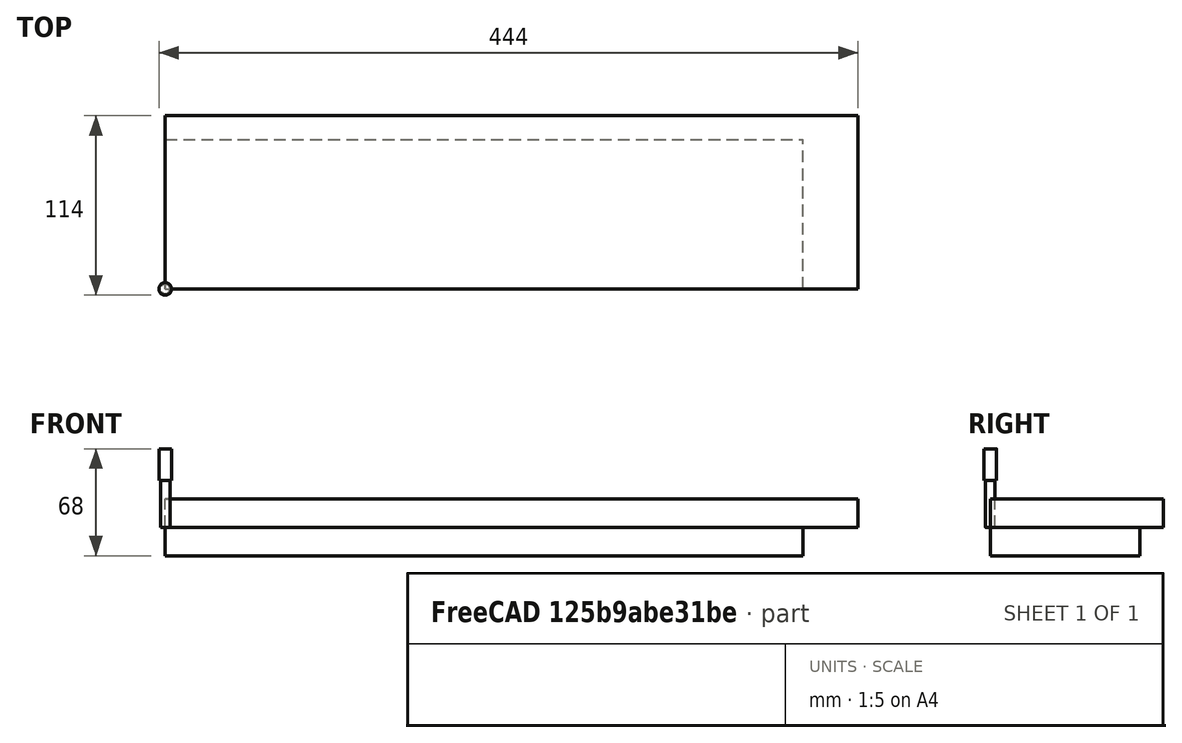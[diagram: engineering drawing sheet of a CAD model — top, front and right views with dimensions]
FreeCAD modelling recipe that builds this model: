
FCSTD DOCUMENT  (FreeCAD 0.22R34789 (Git))
Label: base
License: All rights reserved
LicenseURL: http://en.wikipedia.org/wiki/All_rights_reserved
objects: App::FeaturePython×21, Path::FeaturePython×16, Part::FeaturePython×8, App::DocumentObjectGroup×3, Sketcher::SketchObject×1, PartDesign::Pad×1, PartDesign::Body×1, Mesh::FeaturePython×1
note: 25 computed .brp shape members not serialized (recipe doc carries the construction recipe); baked Part::Feature solids carry a one-line shape summary decoded from their .brp

FEATURE [Sketcher::SketchObject] Sketch
  FullyConstrained = true
  MapMode = 5
  Support = -> [XY_Plane]
  sketch-geometry (4):
    g0: LineSegment StartX=0 StartY=0 StartZ=0 EndX=440 EndY=0 EndZ=0
    g1: LineSegment StartX=440 StartY=0 StartZ=0 EndX=440 EndY=110 EndZ=0
    g2: LineSegment StartX=440 StartY=110 StartZ=0 EndX=0 EndY=110 EndZ=0
    g3: LineSegment StartX=0 StartY=110 StartZ=0 EndX=0 EndY=0 EndZ=0
  constraints (11):
    c: Coincident(g0,g1)
    c: Coincident(g1,g2)
    c: Coincident(g2,g3)
    c: Coincident(g3,g0)
    c: Horizontal(g0)
    c: Horizontal(g2)
    c: Vertical(g1)
    c: Vertical(g3)
    c: Coincident(g0,g-1)
    c: DistanceY(g3,g3) = 110
    c: DistanceX(g2,g2) = 440
FEATURE [PartDesign::Pad] Pad
  Direction = (0,0,1)
  Length = 18
  Length2 = 10
  Profile = -> Sketch
  ReferenceAxis = -> Sketch [N_Axis]
  Type = 0
FEATURE [PartDesign::Body] Body
  Group = -> [Sketch,Pad]
  Origin = -> Origin
  Tip = -> Pad
FEATURE [Part::FeaturePython] Body_001  # a2plus imported part (geometry in sourceFile) (typed FeaturePython)
  a2p_Version = 0.4.61
  fixedPosition = true
  localSourceObject = Body
  objectType = a2pPart
  sourceFile = converted
  subassemblyImport = false
  timeLastImport = 1.69957e+09
  updateColors = true
FEATURE [Part::FeaturePython] b_drill_press_table_001_  label="drill_press_table_base_side_left_001"  # a2plus imported part (geometry in sourceFile) (typed FeaturePython)
  Placement = pos=(362,3.66479e-06,131) rot=(0.57735,-0.57735,0.57735;2.0944rad)
  a2p_Version = 0.4.61
  fixedPosition = false
  objectType = a2pPart
  sourceFile = ./../drill_press_table.FCStd
  sourcePart = base_side_left
  subassemblyImport = false
  timeLastImport = 1.69948e+09
  updateColors = true
FEATURE [Part::FeaturePython] b_drill_press_table_001_001  label="drill_press_table_vacuum_port_001"  # a2plus imported part (geometry in sourceFile) (typed FeaturePython)
  Placement = pos=(310,-276.5,149) rot=(0,-1,0;1.5708rad)
  a2p_Version = 0.4.61
  fixedPosition = false
  objectType = a2pPart
  sourceFile = ./../drill_press_table.FCStd
  sourcePart = vacuum_port
  subassemblyImport = false
  timeLastImport = 1.69948e+09
  updateColors = true
FEATURE [App::FeaturePython] planesParallel_001  label="planesParallel_001__Body_001"  # a2plus constraint (typed FeaturePython)
  Object1 = b_drill_press_table_001_
  Object2 = Body_001
  ParentTreeObject = -> b_drill_press_table_001_
  SubElement1 = Face2
  SubElement2 = Face6
  Suppressed = false
  Type = planesParallel
  directionConstraint = 0
FEATURE [App::FeaturePython] planesParallel_001_mirror  label="planesParallel_001__drill_press_table_base_side_left_001"  # a2plus constraint (typed FeaturePython)
  Object1 = b_drill_press_table_001_
  Object2 = Body_001
  ParentTreeObject = -> Body_001
  SubElement1 = Face2
  SubElement2 = Face6
  Suppressed = false
  Type = planesParallel
  directionConstraint = 0
FEATURE [App::FeaturePython] planesParallel_002  label="planesParallel_002__Body_001"  # a2plus constraint (typed FeaturePython)
  Object1 = b_drill_press_table_001_
  Object2 = Body_001
  ParentTreeObject = -> b_drill_press_table_001_
  SubElement1 = Face3
  SubElement2 = Face1
  Suppressed = false
  Type = planesParallel
  directionConstraint = 0
FEATURE [App::FeaturePython] planesParallel_002_mirror  label="planesParallel_002__drill_press_table_base_side_left_001"  # a2plus constraint (typed FeaturePython)
  Object1 = b_drill_press_table_001_
  Object2 = Body_001
  ParentTreeObject = -> Body_001
  SubElement1 = Face3
  SubElement2 = Face1
  Suppressed = false
  Type = planesParallel
  directionConstraint = 0
FEATURE [App::FeaturePython] planesParallel_003  label="planesParallel_003__Body_001"  # a2plus constraint (typed FeaturePython)
  Object1 = b_drill_press_table_001_
  Object2 = Body_001
  ParentTreeObject = -> b_drill_press_table_001_
  SubElement1 = Face2
  SubElement2 = Face5
  Suppressed = false
  Type = planesParallel
  directionConstraint = 0
FEATURE [App::FeaturePython] planesParallel_003_mirror  label="planesParallel_003__drill_press_table_base_side_left_001"  # a2plus constraint (typed FeaturePython)
  Object1 = b_drill_press_table_001_
  Object2 = Body_001
  ParentTreeObject = -> Body_001
  SubElement1 = Face2
  SubElement2 = Face5
  Suppressed = false
  Type = planesParallel
  directionConstraint = 0
FEATURE [App::FeaturePython] planeCoincident_001  label="planeCoincident_001__Body_001"  # a2plus constraint (typed FeaturePython)
  Object1 = b_drill_press_table_001_
  Object2 = Body_001
  ParentTreeObject = -> b_drill_press_table_001_
  SubElement1 = Face2
  SubElement2 = Face5
  Suppressed = false
  Type = plane
  directionConstraint = 0
  offset = 0
FEATURE [App::FeaturePython] planeCoincident_001_mirror  label="planeCoincident_001__drill_press_table_base_side_left_001"  # a2plus constraint (typed FeaturePython)
  Object1 = b_drill_press_table_001_
  Object2 = Body_001
  ParentTreeObject = -> Body_001
  SubElement1 = Face2
  SubElement2 = Face5
  Suppressed = false
  Type = plane
  directionConstraint = 0
  offset = 0
FEATURE [App::FeaturePython] planeCoincident_002  label="planeCoincident_002__Body_001"  # a2plus constraint (typed FeaturePython)
  Object1 = b_drill_press_table_001_
  Object2 = Body_001
  ParentTreeObject = -> b_drill_press_table_001_
  SubElement1 = Face8
  SubElement2 = Face1
  Suppressed = false
  Type = plane
  directionConstraint = 1
  offset = 0
FEATURE [App::FeaturePython] planeCoincident_002_mirror  label="planeCoincident_002__drill_press_table_base_side_left_001"  # a2plus constraint (typed FeaturePython)
  Object1 = b_drill_press_table_001_
  Object2 = Body_001
  ParentTreeObject = -> Body_001
  SubElement1 = Face8
  SubElement2 = Face1
  Suppressed = false
  Type = plane
  directionConstraint = 1
  offset = 0
FEATURE [App::FeaturePython] planeCoincident_003  label="planeCoincident_003__Body_001"  # a2plus constraint (typed FeaturePython)
  Object1 = b_drill_press_table_001_
  Object2 = Body_001
  ParentTreeObject = -> b_drill_press_table_001_
  SubElement1 = Face1
  SubElement2 = Face4
  Suppressed = false
  Type = plane
  directionConstraint = 1
  offset = 0
FEATURE [App::FeaturePython] planeCoincident_003_mirror  label="planeCoincident_003__drill_press_table_base_side_left_001"  # a2plus constraint (typed FeaturePython)
  Object1 = b_drill_press_table_001_
  Object2 = Body_001
  ParentTreeObject = -> Body_001
  SubElement1 = Face1
  SubElement2 = Face4
  Suppressed = false
  Type = plane
  directionConstraint = 1
  offset = 0
FEATURE [App::FeaturePython] planesParallel_004  label="planesParallel_004__Body_001"  # a2plus constraint (typed FeaturePython)
  Object1 = b_drill_press_table_001_001
  Object2 = Body_001
  ParentTreeObject = -> b_drill_press_table_001_001
  SubElement1 = Face4
  SubElement2 = Face6
  Suppressed = false
  Type = planesParallel
  directionConstraint = 0
FEATURE [App::FeaturePython] planesParallel_004_mirror  label="planesParallel_004__drill_press_table_vacuum_port_001"  # a2plus constraint (typed FeaturePython)
  Object1 = b_drill_press_table_001_001
  Object2 = Body_001
  ParentTreeObject = -> Body_001
  SubElement1 = Face4
  SubElement2 = Face6
  Suppressed = false
  Type = planesParallel
  directionConstraint = 0
FEATURE [App::FeaturePython] planeCoincident_004  label="planeCoincident_004__Body_001"  # a2plus constraint (typed FeaturePython)
  Object1 = b_drill_press_table_001_001
  Object2 = Body_001
  ParentTreeObject = -> b_drill_press_table_001_001
  SubElement1 = Face6
  SubElement2 = Face1
  Suppressed = false
  Type = plane
  directionConstraint = 1
  offset = 0
FEATURE [App::FeaturePython] planeCoincident_004_mirror  label="planeCoincident_004__drill_press_table_vacuum_port_001"  # a2plus constraint (typed FeaturePython)
  Object1 = b_drill_press_table_001_001
  Object2 = Body_001
  ParentTreeObject = -> Body_001
  SubElement1 = Face6
  SubElement2 = Face1
  Suppressed = false
  Type = plane
  directionConstraint = 1
  offset = 0
FEATURE [App::FeaturePython] planeCoincident_005  label="planeCoincident_005__Body_001"  # a2plus constraint (typed FeaturePython)
  Object1 = b_drill_press_table_001_001
  Object2 = Body_001
  ParentTreeObject = -> b_drill_press_table_001_001
  SubElement1 = Face4
  SubElement2 = Face5
  Suppressed = false
  Type = plane
  directionConstraint = 0
  offset = 0
FEATURE [App::FeaturePython] planeCoincident_005_mirror  label="planeCoincident_005__drill_press_table_vacuum_port_001"  # a2plus constraint (typed FeaturePython)
  Object1 = b_drill_press_table_001_001
  Object2 = Body_001
  ParentTreeObject = -> Body_001
  SubElement1 = Face4
  SubElement2 = Face5
  Suppressed = false
  Type = plane
  directionConstraint = 0
  offset = 0
FEATURE [App::FeaturePython] planeCoincident_006  label="planeCoincident_006__drill_press_table_base_side_left_001"  # a2plus constraint (typed FeaturePython)
  Object1 = b_drill_press_table_001_001
  Object2 = b_drill_press_table_001_
  ParentTreeObject = -> b_drill_press_table_001_001
  SubElement1 = Face2
  SubElement2 = Face9
  Suppressed = false
  Type = plane
  directionConstraint = 1
  offset = -10
FEATURE [App::FeaturePython] planeCoincident_006_mirror  label="planeCoincident_006__drill_press_table_vacuum_port_001"  # a2plus constraint (typed FeaturePython)
  Object1 = b_drill_press_table_001_001
  Object2 = b_drill_press_table_001_
  ParentTreeObject = -> b_drill_press_table_001_
  SubElement1 = Face2
  SubElement2 = Face9
  Suppressed = false
  Type = plane
  directionConstraint = 1
  offset = -10
FEATURE [App::FeaturePython] SetupSheet  # Path/CAM operation (typed FeaturePython)
  ClearanceHeightExpression = OpStockZMax+SetupSheet.ClearanceHeightOffset
  ClearanceHeightOffset = 5
  CoolantMode = 0
  CoolantModes = None | Flood | Mist
  FinalDepthExpression = OpFinalDepth
  HorizRapid = 0
  SafeHeightExpression = OpStockZMax+SetupSheet.SafeHeightOffset
  SafeHeightOffset = 3
  StartDepthExpression = OpStartDepth
  StepDownExpression = OpToolDiameter/3
  VertRapid = 0
FEATURE [Part::FeaturePython] Clone  label="Model-drill_press_table_base_side_left_001"  # Draft clone (typed FeaturePython)
  AttacherType = Attacher::AttachEngine3D
  Fuse = false
  Objects = -> [b_drill_press_table_001_]
  PathResource = Model
  Placement = pos=(372,10,113) rot=(0.57735,-0.57735,0.57735;2.0944rad)
  Scale = (1,1,1)
FEATURE [Part::FeaturePython] Clone001  label="Model-drill_press_table_vacuum_port_001"  # Draft clone (typed FeaturePython)
  AttacherType = Attacher::AttachEngine3D
  Fuse = false
  Objects = -> [b_drill_press_table_001_001]
  PathResource = Model
  Placement = pos=(320,-266.5,131) rot=(0,-1,0;1.5708rad)
  Scale = (1,1,1)
FEATURE [App::DocumentObjectGroup] Model
  Group = -> [Clone,Clone001]
FEATURE [Part::FeaturePython] Stock  # WARN: FeaturePython — macro-defined, semantics opaque (R4)
  Base = -> Model
  ExtXneg = 10
  ExtXpos = 10
  ExtYneg = 10
  ExtYpos = 10
  ExtZneg = 0
  ExtZpos = 0
  Placement = pos=(10,10,-18) rot=(0,0,1;0rad)
  StockType = FromBase
FEATURE [Part::FeaturePython] ToolBit001  label="6 mm endmill"  # Path/CAM toolbit (typed FeaturePython)
  BitPropertyNames = Chipload | CuttingEdgeHeight | Diameter | Flutes | Length | Material | ShankDiameter | SpindleDirection
  BitShape = <userpath>/.local/share/FreeCAD/Macro/Tools/Shape/endmill.fcstd
  Chipload = 0
  CuttingEdgeHeight = 30
  Diameter = 6
  File = <userpath>/.local/share/FreeCAD/Macro/Tools/Bit/fbe41074-7b3e-11ee-b334-02422c3495f2.fctb
  Flutes = 2
  Length = 50
  Material = 0
  ShankDiameter = 8
  ShapeName = endmill
  SpindleDirection = 0
FEATURE [Path::FeaturePython] TC__6_mm_endmill  label="TC: 6 mm endmill"  # Path/CAM operation (typed FeaturePython)
  HorizFeed = 20
  HorizRapid = 0
  SpindleDir = 0
  SpindleSpeed = 0
  Tool = -> ToolBit001
  ToolNumber = 16
  VertFeed = 1
  VertRapid = 0
  expr: HorizRapid = SetupSheet.HorizRapid
  expr: VertRapid = SetupSheet.VertRapid
FEATURE [Path::FeaturePython] Pocket_Shape  # Path/CAM operation (typed FeaturePython)
  Active = true
  AreaParams:
    Tolerance = 1e-07
    FitArcs = True
    Simplify = False
    CleanDistance = 0.0
    Accuracy = 0.01
    Unit = 1.0
    MinArcPoints = 4
    MaxArcPoints = 100
    ClipperScale = 10000000.0
    Fill = 0
    Coplanar = 0
    Reorient = True
    Outline = False
    Explode = False
    OpenMode = 0
    Deflection = 0.01
    SubjectFill = 0
    ClipFill = 0
    Offset = 0.0
    ExtraPass = 0
    Stepover = 0.0
    LastStepover = 0.0
    JoinType = 0
    EndType = 0
    MiterLimit = 2.0
    RoundPrecision = 0.0
    PocketMode = 2
    ToolRadius = 3.0
    PocketExtraOffset = -1.0
    PocketStepover = 4.800000000000001
    PocketLastStepover = 0.0
    FromCenter = True
    Angle = 45.0
    AngleShift = 0.0
    Shift = 0.0
    Thicken = False
    SectionCount = -1
    Stepdown = 1.0
    SectionOffset = 0.0
    SectionTolerance = 1e-07
    SectionMode = 2
    Project = False
  Base = -> [Clone]
  ClearanceHeight = 5
  CoolantMode = 0
  CutMode = 0
  CycleTime = 00:08:09
  ExtensionCorners = true
  ExtensionFeature = -> [Clone]
  ExtensionLengthDefault = 3
  ExtraOffset = -1
  FinalDepth = -6.5
  FinishDepth = 0
  KeepToolDown = false
  MinTravel = false
  OffsetPattern = 1
  OpFinalDepth = -6
  OpStartDepth = 9.95e-14
  OpStockZMax = 8.17e-14
  OpStockZMin = -18
  OpToolDiameter = 6
  PathParams = {'orientation': 1, 'feedrate': 20.0, 'feedrate_v': 1.0, 'verbose': True, 'resume_height': 3.0000000000000817, 'retraction': 5.000000000000082, 'return_end': True, 'preamble': False}
  PocketLastStepOver = 0
  SafeHeight = 3
  SplitArcs = false
  StartAt = 0
  StartDepth = 9.95e-14
  StartPoint = (0,0,0)
  StepDown = 2
  StepOver = 80
  ToolController = -> TC__6_mm_endmill
  UseOutline = false
  UseRestMachining = false
  UseStartPoint = false
  ZigZagAngle = 45
  expr: ClearanceHeight = OpStockZMax + SetupSheet.ClearanceHeightOffset
  expr: ExtensionLengthDefault = OpToolDiameter / 2
  expr: FinalDepth = OpFinalDepth - 0.5 mm
  expr: SafeHeight = OpStockZMax + SetupSheet.SafeHeightOffset
  expr: StartDepth = OpStartDepth
  expr: StepDown = OpToolDiameter / 3
FEATURE [Path::FeaturePython] Pocket_Shape001  # Path/CAM operation (typed FeaturePython)
  Active = true
  AreaParams:
    Tolerance = 1e-07
    FitArcs = True
    Simplify = False
    CleanDistance = 0.0
    Accuracy = 0.01
    Unit = 1.0
    MinArcPoints = 4
    MaxArcPoints = 100
    ClipperScale = 10000000.0
    Fill = 0
    Coplanar = 0
    Reorient = True
    Outline = False
    Explode = False
    OpenMode = 0
    Deflection = 0.01
    SubjectFill = 0
    ClipFill = 0
    Offset = 0.0
    ExtraPass = 0
    Stepover = 0.0
    LastStepover = 0.0
    JoinType = 0
    EndType = 0
    MiterLimit = 2.0
    RoundPrecision = 0.0
    PocketMode = 2
    ToolRadius = 3.0
    PocketExtraOffset = -0.8
    PocketStepover = 4.800000000000001
    PocketLastStepover = 0.0
    FromCenter = True
    Angle = 45.0
    AngleShift = 0.0
    Shift = 0.0
    Thicken = False
    SectionCount = -1
    Stepdown = 1.0
    SectionOffset = 0.0
    SectionTolerance = 1e-07
    SectionMode = 2
    Project = False
  Base = -> [Clone]
  ClearanceHeight = 5
  CoolantMode = 0
  CutMode = 0
  CycleTime = 00:06:03
  ExtensionCorners = true
  ExtensionFeature = -> [Clone]
  ExtensionLengthDefault = 4
  ExtraOffset = -0.8
  FinalDepth = -6.5
  FinishDepth = 0
  KeepToolDown = false
  MinTravel = false
  OffsetPattern = 1
  OpFinalDepth = -6
  OpStartDepth = 9.95e-14
  OpStockZMax = 8.17e-14
  OpStockZMin = -18
  OpToolDiameter = 6
  PathParams = {'orientation': 1, 'feedrate': 20.0, 'feedrate_v': 1.0, 'verbose': True, 'resume_height': 3.0000000000000817, 'retraction': 5.000000000000082, 'return_end': True, 'preamble': False}
  PocketLastStepOver = 0
  SafeHeight = 3
  SplitArcs = false
  StartAt = 0
  StartDepth = 9.95e-14
  StartPoint = (0,0,0)
  StepDown = 2
  StepOver = 80
  ToolController = -> TC__6_mm_endmill
  UseOutline = false
  UseRestMachining = false
  UseStartPoint = false
  ZigZagAngle = 45
  expr: ClearanceHeight = OpStockZMax + SetupSheet.ClearanceHeightOffset
  expr: ExtensionLengthDefault = OpToolDiameter / 2 + 1 mm
  expr: FinalDepth = OpFinalDepth - 0.5 mm
  expr: SafeHeight = OpStockZMax + SetupSheet.SafeHeightOffset
  expr: StartDepth = OpStartDepth
  expr: StepDown = OpToolDiameter / 3
FEATURE [Path::FeaturePython] Pocket_Shape002  # Path/CAM operation (typed FeaturePython)
  Active = true
  AreaParams:
    Tolerance = 1e-07
    FitArcs = True
    Simplify = False
    CleanDistance = 0.0
    Accuracy = 0.01
    Unit = 1.0
    MinArcPoints = 4
    MaxArcPoints = 100
    ClipperScale = 10000000.0
    Fill = 0
    Coplanar = 0
    Reorient = True
    Outline = False
    Explode = False
    OpenMode = 0
    Deflection = 0.01
    SubjectFill = 0
    ClipFill = 0
    Offset = 0.0
    ExtraPass = 0
    Stepover = 0.0
    LastStepover = 0.0
    JoinType = 0
    EndType = 0
    MiterLimit = 2.0
    RoundPrecision = 0.0
    PocketMode = 2
    ToolRadius = 3.0
    PocketExtraOffset = -0.6
    PocketStepover = 4.800000000000001
    PocketLastStepover = 0.0
    FromCenter = True
    Angle = 45.0
    AngleShift = 0.0
    Shift = 0.0
    Thicken = False
    SectionCount = -1
    Stepdown = 1.0
    SectionOffset = 0.0
    SectionTolerance = 1e-07
    SectionMode = 2
    Project = False
  Base = -> [Clone]
  ClearanceHeight = 5
  CoolantMode = 0
  CutMode = 0
  CycleTime = 00:06:39
  ExtensionCorners = true
  ExtensionFeature = -> [Clone]
  ExtensionLengthDefault = 3
  ExtraOffset = -0.6
  FinalDepth = -6.5
  FinishDepth = 0
  KeepToolDown = false
  MinTravel = false
  OffsetPattern = 1
  OpFinalDepth = -6
  OpStartDepth = 8.17e-14
  OpStockZMax = 8.17e-14
  OpStockZMin = -18
  OpToolDiameter = 6
  PathParams = {'orientation': 1, 'feedrate': 20.0, 'feedrate_v': 1.0, 'verbose': True, 'resume_height': 3.0000000000000817, 'retraction': 5.000000000000082, 'return_end': True, 'preamble': False}
  PocketLastStepOver = 0
  SafeHeight = 3
  SplitArcs = false
  StartAt = 0
  StartDepth = 8.17e-14
  StartPoint = (0,0,0)
  StepDown = 2
  StepOver = 80
  ToolController = -> TC__6_mm_endmill
  UseOutline = false
  UseRestMachining = false
  UseStartPoint = false
  ZigZagAngle = 45
  expr: ClearanceHeight = OpStockZMax + SetupSheet.ClearanceHeightOffset
  expr: ExtensionLengthDefault = OpToolDiameter / 2
  expr: FinalDepth = OpFinalDepth - 0.5 mm
  expr: SafeHeight = OpStockZMax + SetupSheet.SafeHeightOffset
  expr: StartDepth = OpStartDepth
  expr: StepDown = OpToolDiameter / 3
FEATURE [Path::FeaturePython] Profile  # Path/CAM operation (typed FeaturePython)
  Active = true
  AreaParams:
    Tolerance = 1e-07
    FitArcs = True
    Simplify = False
    CleanDistance = 0.0
    Accuracy = 0.01
    Unit = 1.0
    MinArcPoints = 4
    MaxArcPoints = 100
    ClipperScale = 10000000.0
    Fill = 0
    Coplanar = 0
    Reorient = True
    Outline = False
    Explode = False
    OpenMode = 0
    Deflection = 0.01
    SubjectFill = 0
    ClipFill = 0
    Offset = -3.0
    ExtraPass = 0
    Stepover = 0.0
    LastStepover = 0.0
    JoinType = 0
    EndType = 0
    MiterLimit = 2.0
    RoundPrecision = 0.0
    PocketMode = 0
    ToolRadius = 1.0
    PocketExtraOffset = 0.0
    PocketStepover = 0.0
    PocketLastStepover = 0.0
    FromCenter = False
    Angle = 45.0
    AngleShift = 0.0
    Shift = 0.0
    Thicken = False
    SectionCount = -1
    Stepdown = 1.0
    SectionOffset = 0.0
    SectionTolerance = 1e-07
    SectionMode = 2
    Project = False
  Base = -> [Clone]
  ClearanceHeight = 5
  CoolantMode = 0
  CycleTime = 00:01:40
  Direction = 0
  FinalDepth = -19.5
  HandleMultipleFeatures = 0
  JoinType = 0
  MiterLimit = 0.1
  OffsetExtra = 0
  OpFinalDepth = -18
  OpStartDepth = 8.17e-14
  OpStockZMax = 8.17e-14
  OpStockZMin = -18
  OpToolDiameter = 6
  PathParams = {'orientation': 1, 'feedrate': 20.0, 'feedrate_v': 1.0, 'verbose': True, 'resume_height': 3.0000000000000817, 'retraction': 5.000000000000082, 'return_end': True, 'preamble': False}
  SafeHeight = 3
  Side = 1
  SplitArcs = false
  StartDepth = 8.17e-14
  StartPoint = (0,0,0)
  StepDown = 2
  ToolController = -> TC__6_mm_endmill
  UseComp = true
  UseStartPoint = false
  processCircles = false
  processHoles = false
  processPerimeter = true
  expr: ClearanceHeight = OpStockZMax + SetupSheet.ClearanceHeightOffset
  expr: FinalDepth = OpFinalDepth - 1.5 mm
  expr: SafeHeight = OpStockZMax + SetupSheet.SafeHeightOffset
  expr: StartDepth = OpStartDepth
  expr: StepDown = OpToolDiameter / 3
FEATURE [Path::FeaturePython] DressupTag  # Path/CAM operation (typed FeaturePython)
  Angle = 45
  Base = -> Profile
  Height = 8
  Positions = (2) [(78.7968,34.3275,0),(40.6906,55.077,0)]
  Radius = 0
  SegmentationFactor = 50
  Width = 4.92
FEATURE [Path::FeaturePython] Profile001  # Path/CAM operation (typed FeaturePython)
  Active = true
  AreaParams:
    Tolerance = 1e-07
    FitArcs = True
    Simplify = False
    CleanDistance = 0.0
    Accuracy = 0.01
    Unit = 1.0
    MinArcPoints = 4
    MaxArcPoints = 100
    ClipperScale = 10000000.0
    Fill = 0
    Coplanar = 0
    Reorient = True
    Outline = False
    Explode = False
    OpenMode = 0
    Deflection = 0.01
    SubjectFill = 0
    ClipFill = 0
    Offset = 3.0
    ExtraPass = 0
    Stepover = 0.0
    LastStepover = 0.0
    JoinType = 0
    EndType = 0
    MiterLimit = 2.0
    RoundPrecision = 0.0
    PocketMode = 0
    ToolRadius = 1.0
    PocketExtraOffset = 0.0
    PocketStepover = 0.0
    PocketLastStepover = 0.0
    FromCenter = False
    Angle = 45.0
    AngleShift = 0.0
    Shift = 0.0
    Thicken = False
    SectionCount = -1
    Stepdown = 1.0
    SectionOffset = 0.0
    SectionTolerance = 1e-07
    SectionMode = 2
    Project = False
  Base = -> [Clone]
  ClearanceHeight = 5
  CoolantMode = 0
  CycleTime = 00:07:32
  Direction = 0
  FinalDepth = -19.5
  HandleMultipleFeatures = 0
  JoinType = 0
  MiterLimit = 0.1
  OffsetExtra = 0
  OpFinalDepth = -18
  OpStartDepth = 8.17e-14
  OpStockZMax = 8.17e-14
  OpStockZMin = -18
  OpToolDiameter = 6
  PathParams = {'orientation': 1, 'feedrate': 20.0, 'feedrate_v': 1.0, 'verbose': True, 'resume_height': 3.0000000000000817, 'retraction': 5.000000000000082, 'return_end': True, 'preamble': False}
  SafeHeight = 3
  Side = 0
  SplitArcs = false
  StartDepth = 8.17e-14
  StartPoint = (0,0,0)
  StepDown = 2
  ToolController = -> TC__6_mm_endmill
  UseComp = true
  UseStartPoint = false
  processCircles = false
  processHoles = false
  processPerimeter = true
  expr: ClearanceHeight = OpStockZMax + SetupSheet.ClearanceHeightOffset
  expr: FinalDepth = OpFinalDepth - 1.5 mm
  expr: SafeHeight = OpStockZMax + SetupSheet.SafeHeightOffset
  expr: StartDepth = OpStartDepth
  expr: StepDown = OpToolDiameter / 3
FEATURE [Path::FeaturePython] DressupTag001  # Path/CAM operation (typed FeaturePython)
  Angle = 45
  Base = -> Profile001
  Height = 8
  Positions = (4) [(235,7.00001,0),(85,7.00001,0),(85,88,0),(235,88,0)]
  Radius = 0
  SegmentationFactor = 50
  Width = 12
FEATURE [Path::FeaturePython] Pocket_Shape003  # Path/CAM operation (typed FeaturePython)
  Active = true
  AreaParams:
    Tolerance = 1e-07
    FitArcs = True
    Simplify = False
    CleanDistance = 0.0
    Accuracy = 0.01
    Unit = 1.0
    MinArcPoints = 4
    MaxArcPoints = 100
    ClipperScale = 10000000.0
    Fill = 0
    Coplanar = 0
    Reorient = True
    Outline = False
    Explode = False
    OpenMode = 0
    Deflection = 0.01
    SubjectFill = 0
    ClipFill = 0
    Offset = 0.0
    ExtraPass = 0
    Stepover = 0.0
    LastStepover = 0.0
    JoinType = 0
    EndType = 0
    MiterLimit = 2.0
    RoundPrecision = 0.0
    PocketMode = 2
    ToolRadius = 3.0
    PocketExtraOffset = 0.0
    PocketStepover = 4.800000000000001
    PocketLastStepover = 0.0
    FromCenter = True
    Angle = 45.0
    AngleShift = 0.0
    Shift = 0.0
    Thicken = False
    SectionCount = -1
    Stepdown = 1.0
    SectionOffset = 0.0
    SectionTolerance = 1e-07
    SectionMode = 2
    Project = False
  Base = -> [Clone001]
  ClearanceHeight = 5
  CoolantMode = 0
  CutMode = 0
  CycleTime = 00:02:08
  ExtensionCorners = true
  ExtensionFeature = -> [Clone001]
  ExtensionLengthDefault = 3
  ExtraOffset = 0
  FinalDepth = -4
  FinishDepth = 0
  KeepToolDown = false
  MinTravel = false
  OffsetPattern = 1
  OpFinalDepth = -4
  OpStartDepth = 8.17e-14
  OpStockZMax = 8.17e-14
  OpStockZMin = -18
  OpToolDiameter = 6
  PathParams = {'orientation': 1, 'feedrate': 20.0, 'feedrate_v': 1.0, 'verbose': True, 'resume_height': 3.0000000000000817, 'retraction': 5.000000000000082, 'return_end': True, 'preamble': False}
  PocketLastStepOver = 0
  SafeHeight = 3
  SplitArcs = false
  StartAt = 0
  StartDepth = 8.17e-14
  StartPoint = (0,0,0)
  StepDown = 2
  StepOver = 80
  ToolController = -> TC__6_mm_endmill
  UseOutline = false
  UseRestMachining = false
  UseStartPoint = false
  ZigZagAngle = 45
  expr: ClearanceHeight = OpStockZMax + SetupSheet.ClearanceHeightOffset
  expr: ExtensionLengthDefault = OpToolDiameter / 2
  expr: FinalDepth = OpFinalDepth
  expr: SafeHeight = OpStockZMax + SetupSheet.SafeHeightOffset
  expr: StartDepth = OpStartDepth
  expr: StepDown = OpToolDiameter / 3
FEATURE [Path::FeaturePython] Profile002  # Path/CAM operation (typed FeaturePython)
  Active = true
  AreaParams:
    Tolerance = 1e-07
    FitArcs = True
    Simplify = False
    CleanDistance = 0.0
    Accuracy = 0.01
    Unit = 1.0
    MinArcPoints = 4
    MaxArcPoints = 100
    ClipperScale = 10000000.0
    Fill = 0
    Coplanar = 0
    Reorient = True
    Outline = False
    Explode = False
    OpenMode = 0
    Deflection = 0.01
    SubjectFill = 0
    ClipFill = 0
    Offset = -3.0
    ExtraPass = 0
    Stepover = 0.0
    LastStepover = 0.0
    JoinType = 0
    EndType = 0
    MiterLimit = 2.0
    RoundPrecision = 0.0
    PocketMode = 0
    ToolRadius = 1.0
    PocketExtraOffset = 0.0
    PocketStepover = 0.0
    PocketLastStepover = 0.0
    FromCenter = False
    Angle = 45.0
    AngleShift = 0.0
    Shift = 0.0
    Thicken = False
    SectionCount = -1
    Stepdown = 1.0
    SectionOffset = 0.0
    SectionTolerance = 1e-07
    SectionMode = 2
    Project = False
  Base = -> [Clone001]
  ClearanceHeight = 5
  CoolantMode = 0
  CycleTime = 00:01:33
  Direction = 0
  FinalDepth = -19.5
  HandleMultipleFeatures = 0
  JoinType = 0
  MiterLimit = 0.1
  OffsetExtra = 0
  OpFinalDepth = -18
  OpStartDepth = 8.17e-14
  OpStockZMax = 8.17e-14
  OpStockZMin = -18
  OpToolDiameter = 6
  PathParams = {'orientation': 1, 'feedrate': 20.0, 'feedrate_v': 1.0, 'verbose': True, 'resume_height': 3.0000000000000817, 'retraction': 5.000000000000082, 'return_end': True, 'preamble': False}
  SafeHeight = 3
  Side = 1
  SplitArcs = false
  StartDepth = 8.17e-14
  StartPoint = (0,0,0)
  StepDown = 2
  ToolController = -> TC__6_mm_endmill
  UseComp = true
  UseStartPoint = false
  processCircles = false
  processHoles = false
  processPerimeter = true
  expr: ClearanceHeight = OpStockZMax + SetupSheet.ClearanceHeightOffset
  expr: FinalDepth = OpFinalDepth - 1.5 mm
  expr: SafeHeight = OpStockZMax + SetupSheet.SafeHeightOffset
  expr: StartDepth = OpStartDepth
  expr: StepDown = OpToolDiameter / 3
FEATURE [Path::FeaturePython] DressupTag002  # Path/CAM operation (typed FeaturePython)
  Angle = 45
  Base = -> Profile002
  Disabled = [0]
  Height = 8
  Positions = (2) [(356.149,20.5348,0),(347.726,72.6677,0)]
  Radius = 0
  SegmentationFactor = 50
  Width = 10
FEATURE [Path::FeaturePython] Profile003  # Path/CAM operation (typed FeaturePython)
  Active = true
  AreaParams:
    Tolerance = 1e-07
    FitArcs = True
    Simplify = False
    CleanDistance = 0.0
    Accuracy = 0.01
    Unit = 1.0
    MinArcPoints = 4
    MaxArcPoints = 100
    ClipperScale = 10000000.0
    Fill = 0
    Coplanar = 0
    Reorient = True
    Outline = False
    Explode = False
    OpenMode = 0
    Deflection = 0.01
    SubjectFill = 0
    ClipFill = 0
    Offset = 3.0
    ExtraPass = 0
    Stepover = 0.0
    LastStepover = 0.0
    JoinType = 0
    EndType = 0
    MiterLimit = 2.0
    RoundPrecision = 0.0
    PocketMode = 0
    ToolRadius = 1.0
    PocketExtraOffset = 0.0
    PocketStepover = 0.0
    PocketLastStepover = 0.0
    FromCenter = False
    Angle = 45.0
    AngleShift = 0.0
    Shift = 0.0
    Thicken = False
    SectionCount = -1
    Stepdown = 1.0
    SectionOffset = 0.0
    SectionTolerance = 1e-07
    SectionMode = 2
    Project = False
  Base = -> [Clone001]
  ClearanceHeight = 5
  CoolantMode = 0
  CycleTime = 00:03:50
  Direction = 0
  FinalDepth = -19.5
  HandleMultipleFeatures = 0
  JoinType = 0
  MiterLimit = 0.1
  OffsetExtra = 0
  OpFinalDepth = -18
  OpStartDepth = 8.17e-14
  OpStockZMax = 8.17e-14
  OpStockZMin = -18
  OpToolDiameter = 6
  PathParams = {'orientation': 1, 'feedrate': 20.0, 'feedrate_v': 1.0, 'verbose': True, 'resume_height': 3.0000000000000817, 'retraction': 5.000000000000082, 'return_end': True, 'preamble': False}
  SafeHeight = 3
  Side = 0
  SplitArcs = false
  StartDepth = 8.17e-14
  StartPoint = (0,0,0)
  StepDown = 2
  ToolController = -> TC__6_mm_endmill
  UseComp = true
  UseStartPoint = false
  processCircles = false
  processHoles = false
  processPerimeter = true
  expr: ClearanceHeight = OpStockZMax + SetupSheet.ClearanceHeightOffset
  expr: FinalDepth = OpFinalDepth - 1.5 mm
  expr: SafeHeight = OpStockZMax + SetupSheet.SafeHeightOffset
  expr: StartDepth = OpStartDepth
  expr: StepDown = OpToolDiameter / 3
FEATURE [Path::FeaturePython] DressupTag003  # Path/CAM operation (typed FeaturePython)
  Angle = 45
  Base = -> Profile003
  Height = 8
  Positions = (4) [(398,47.5,0),(357.5,7,0),(317,47.5,0),(357.5,88,0)]
  Radius = 0
  SegmentationFactor = 50
  Width = 7.5
FEATURE [Part::FeaturePython] ToolBit  label="Endmill D=3.9 (4.0), H=9.5, S=8"  # Path/CAM toolbit (typed FeaturePython)
  BitPropertyNames = Chipload | CuttingEdgeHeight | Diameter | Flutes | Length | Material | ShankDiameter | SpindleDirection
  BitShape = <userpath>/.local/share/FreeCAD/Macro/Tools/Shape/endmill.fcstd
  Chipload = 0
  CuttingEdgeHeight = 19
  Diameter = 3.9
  File = <userpath>/.local/share/FreeCAD/Macro/Tools/Bit/2366a052-8063-11ee-b9a7-8ca982cd3061.fctb
  Flutes = 1
  Length = 50
  Material = 0
  ShankDiameter = 8
  ShapeName = endmill
  SpindleDirection = 0
FEATURE [Path::FeaturePython] TC__Endmill_D_3_9__4_0___H_9_5__S_8  label="TC: Endmill D=3.9 (4.0), H=9.5, S=8"  # Path/CAM operation (typed FeaturePython)
  HorizFeed = 10
  HorizRapid = 0
  SpindleDir = 0
  SpindleSpeed = 0
  Tool = -> ToolBit
  ToolNumber = 20
  VertFeed = 1
  VertRapid = 0
  expr: HorizRapid = SetupSheet.HorizRapid
  expr: VertRapid = SetupSheet.VertRapid
FEATURE [App::DocumentObjectGroup] Tools
  Group = -> [TC__6_mm_endmill,TC__Endmill_D_3_9__4_0___H_9_5__S_8]
FEATURE [Path::FeaturePython] Profile004  label="4mm_otwory"  # Path/CAM operation (typed FeaturePython)
  Active = true
  AreaParams:
    Tolerance = 1e-07
    FitArcs = True
    Simplify = False
    CleanDistance = 0.0
    Accuracy = 0.01
    Unit = 1.0
    MinArcPoints = 4
    MaxArcPoints = 100
    ClipperScale = 10000000.0
    Fill = 0
    Coplanar = 0
    Reorient = True
    Outline = False
    Explode = False
    OpenMode = 0
    Deflection = 0.01
    SubjectFill = 0
    ClipFill = 0
    Offset = -1.95
    ExtraPass = 0
    Stepover = 0.0
    LastStepover = 0.0
    JoinType = 0
    EndType = 0
    MiterLimit = 2.0
    RoundPrecision = 0.0
    PocketMode = 0
    ToolRadius = 1.0
    PocketExtraOffset = 0.0
    PocketStepover = 0.0
    PocketLastStepover = 0.0
    FromCenter = False
    Angle = 45.0
    AngleShift = 0.0
    Shift = 0.0
    Thicken = False
    SectionCount = -1
    Stepdown = 1.0
    SectionOffset = 0.0
    SectionTolerance = 1e-07
    SectionMode = 2
    Project = False
  Base = -> [Clone001]
  ClearanceHeight = 5
  CoolantMode = 0
  CycleTime = 00:10:12
  Direction = 0
  FinalDepth = -8
  HandleMultipleFeatures = 0
  JoinType = 0
  MiterLimit = 0.1
  OffsetExtra = 0
  OpFinalDepth = -18
  OpStartDepth = 8.17e-14
  OpStockZMax = 8.17e-14
  OpStockZMin = -18
  OpToolDiameter = 3.9
  PathParams = {'orientation': 1, 'feedrate': 10.0, 'feedrate_v': 1.0, 'verbose': True, 'resume_height': 3.0000000000000817, 'retraction': 5.000000000000082, 'return_end': True, 'preamble': False}
  SafeHeight = 3
  Side = 1
  SplitArcs = false
  StartDepth = 8.17e-14
  StartPoint = (0,0,0)
  StepDown = 1.3
  ToolController = -> TC__Endmill_D_3_9__4_0___H_9_5__S_8
  UseComp = true
  UseStartPoint = false
  processCircles = false
  processHoles = false
  processPerimeter = true
  expr: ClearanceHeight = OpStockZMax + SetupSheet.ClearanceHeightOffset
  expr: FinalDepth = OpFinalDepth + 10 mm
  expr: SafeHeight = OpStockZMax + SetupSheet.SafeHeightOffset
  expr: StartDepth = OpStartDepth
  expr: StepDown = OpToolDiameter / 3
FEATURE [App::DocumentObjectGroup] Operations
  Group = -> [Pocket_Shape,Pocket_Shape001,Pocket_Shape002,DressupTag,DressupTag001,Pocket_Shape003,DressupTag002,DressupTag003,Profile004]
FEATURE [Path::FeaturePython] Job  # Path/CAM operation (typed FeaturePython)
  CycleTime = 00:47:46
  Fixtures = G54
  GeometryTolerance = 0.01
  JobType = 0
  Model = -> Model
  Operations = -> Operations
  OrderOutputBy = 0
  PostProcessor = 3
  PostProcessorOutputFile = %D/%d
  SetupSheet = -> SetupSheet
  SplitOutput = false
  Stock = -> Stock
  Tools = -> Tools
FEATURE [Mesh::FeaturePython] CutMaterial  # WARN: FeaturePython — macro-defined, semantics opaque (R4)
